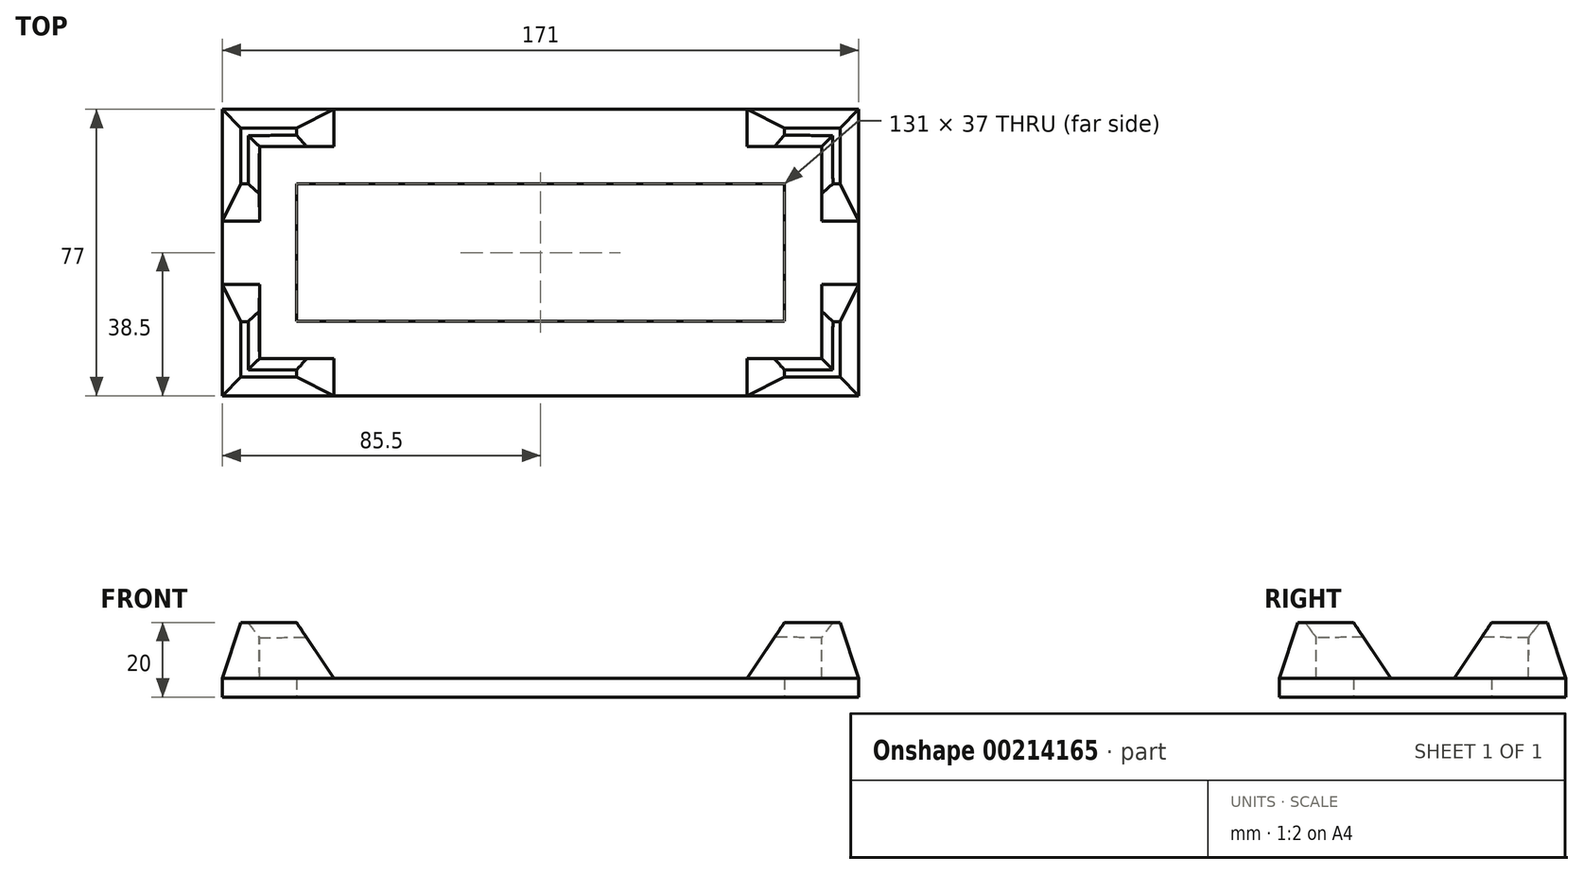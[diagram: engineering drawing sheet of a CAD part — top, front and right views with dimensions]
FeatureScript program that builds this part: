
annotation { "Feature Type Name" : "Feature", "Feature Type Description" : "" }
export const myFeature = defineFeature(function(context is Context, id is Id, definition is map)
    precondition{}
    {
        {
            var Q0;
            Q0=qCreatedBy(makeId("Top.planeOp"),FACE);
            var sketch = newSketch(context, id + "F0", { "sketchPlane" : qUnion([Q0])});
            skLineSegment(sketch, "E0.bottom", {"start": v(75.5, -28.5) * mm, "end": v(-75.5, -28.5) * mm, "construction": true});
            skLineSegment(sketch, "E0.top", {"start": v(75.5, 28.5) * mm, "end": v(-75.5, 28.5) * mm, "construction": true});
            skLineSegment(sketch, "E0.left", {"start": v(75.5, -28.5) * mm, "end": v(75.5, 28.5) * mm, "construction": true});
            skLineSegment(sketch, "E0.right", {"start": v(-75.5, -28.5) * mm, "end": v(-75.5, 28.5) * mm, "construction": true});
            skPoint(sketch, "E0.middle", {"position": v(0, 0) * mm});
            skLineSegment(sketch, "E1.bottom", {"start": v(85.5, -38.5) * mm, "end": v(-85.5, -38.5) * mm});
            skLineSegment(sketch, "E1.top", {"start": v(85.5, 38.5) * mm, "end": v(-85.5, 38.5) * mm});
            skLineSegment(sketch, "E1.left", {"start": v(85.5, -38.5) * mm, "end": v(85.5, 38.5) * mm});
            skLineSegment(sketch, "E1.right", {"start": v(-85.5, -38.5) * mm, "end": v(-85.5, 38.5) * mm});
            skSolve(sketch);
        }
        {
            var Q0;
            Q0=qCreatedBy(makeId("Top.planeOp"),FACE);
            cPlane(context, id + "F1", {"entities" : qUnion([Q0]), "cplaneType" : CPlaneType.OFFSET, "offset" : 15 * mm, "width" : 150 * mm, "height" : 150 * mm});
        }
        {
            var Q0;
            Q0=qCreatedBy(id+"F1.planeOp",FACE);
            var sketch = newSketch(context, id + "F2", { "sketchPlane" : qUnion([Q0])});
            skPoint(sketch, "E2.0", {"position": v(-85.5, -38.5) * mm});
            skPoint(sketch, "E3.0", {"position": v(-75.5, -28.5) * mm});
            skLineSegment(sketch, "E4", {"start": v(-75.58, -18.5) * mm, "end": v(-75.5, -28.5) * mm});
            skLineSegment(sketch, "E5", {"start": v(-75.5, -28.5) * mm, "end": v(-85.5, -38.5) * mm, "construction": true});
            skPoint(sketch, "E6", {"position": v(-80.5, -33.5) * mm});
            skLineSegment(sketch, "E7", {"start": v(-75.58, -18.5) * mm, "end": v(-80.5, -18.54) * mm});
            skLineSegment(sketch, "E8", {"start": v(-80.5, -18.54) * mm, "end": v(-80.5, -33.5) * mm});
            skLineSegment(sketch, "E9.MirrorCS", {"start": v(-65.54, -33.5) * mm, "end": v(-80.5, -33.5) * mm});
            skLineSegment(sketch, "E10.MirrorCS", {"start": v(-65.5, -28.58) * mm, "end": v(-65.54, -33.5) * mm});
            skLineSegment(sketch, "E11.MirrorCS", {"start": v(-65.5, -28.58) * mm, "end": v(-75.5, -28.5) * mm});
            skSolve(sketch);
        }
        {
            var Q0;
            Q0=qCreatedBy(makeId("Top.planeOp"),FACE);
            var sketch = newSketch(context, id + "F3", { "sketchPlane" : qUnion([Q0])});
            skPoint(sketch, "E12.0", {"position": v(-85.5, -38.5) * mm});
            skPoint(sketch, "E13.0", {"position": v(-75.5, -28.5) * mm});
            skLineSegment(sketch, "E14", {"start": v(-85.5, -38.5) * mm, "end": v(-85.5, -8.5) * mm});
            skLineSegment(sketch, "E15", {"start": v(-85.5, -8.5) * mm, "end": v(-75.5, -8.5) * mm});
            skLineSegment(sketch, "E16", {"start": v(-75.5, -8.5) * mm, "end": v(-75.5, -28.5) * mm});
            skLineSegment(sketch, "E17", {"start": v(-75.5, -28.5) * mm, "end": v(-85.5, -38.5) * mm, "construction": true});
            skLineSegment(sketch, "E18.MirrorCS", {"start": v(-55.5, -28.5) * mm, "end": v(-75.5, -28.5) * mm});
            skLineSegment(sketch, "E19.MirrorCS", {"start": v(-85.5, -38.5) * mm, "end": v(-55.5, -38.5) * mm});
            skLineSegment(sketch, "E20.MirrorCS", {"start": v(-55.5, -38.5) * mm, "end": v(-55.5, -28.5) * mm});
            skSolve(sketch);
        }
        {
            var Q0;
            Q0=makeQuery(id+"F0.imprint","IMPRINT",FACE,{"disambiguationData":[TD([[makeQuery(id+"F0.imprint","IMPRINT",EDGE,{"derivedFrom":sQuery(id+"F0.wireOp",EDGE,"E1.bottom")}),-1.0]])]});
            extrude(context, id + "F4", {"entities" : qUnion([Q0]), "oppositeDirection" : true, "depth" : 5 * mm});
        }
        {
            var Q1;
            Q1=makeQuery(id+"F3.imprint","IMPRINT",FACE,{"disambiguationData":[TD([[makeQuery(id+"F3.imprint","IMPRINT",EDGE,{"derivedFrom":sQuery(id+"F3.wireOp",EDGE,"E14")}),-1.0]])]});
            var Q2;
            Q2=makeQuery(id+"F2.imprint","IMPRINT",FACE,{"disambiguationData":[TD([[makeQuery(id+"F2.imprint","IMPRINT",EDGE,{"derivedFrom":sQuery(id+"F2.wireOp",EDGE,"E4")}),-1.0]])]});
            loft(context, id + "F5", {"operationType" : NewBodyOperationType.ADD, "sheetProfilesArray" : [{ "sheetProfileEntities" : qUnion([Q1]) }, { "sheetProfileEntities" : qUnion([Q2]) }]});
        }
        {
            var Q0;
            Q0=makeQuery(id+"F5.opLoft","MID_CAP_EDGE",EDGE,{"disambiguationData":[OSD([sQuery(id+"F2.wireOp",EDGE,"E4"),sQuery(id+"F2.wireOp",EDGE,"E7"),sQuery(id+"F2.wireOp",EDGE,"E11.MirrorCS")])],"capPos":1.0});
            var Q1;
            Q1=makeQuery(id+"F5.opLoft","MID_CAP_EDGE",EDGE,{"disambiguationData":[OSD([sQuery(id+"F2.wireOp",EDGE,"E4"),sQuery(id+"F2.wireOp",EDGE,"E10.MirrorCS"),sQuery(id+"F2.wireOp",EDGE,"E11.MirrorCS")])],"capPos":1.0});
            chamfer(context, id + "F6", {"entities" : qUnion([Q0, Q1]), "chamferType" : ChamferType.TWO_OFFSETS, "width1" : 3 * mm, "oppositeDirection" : false, "width2" : 4 * mm, "tangentPropagation" : true});
        }
        {
            var Q0;
            Q0=makeQuery(id+"F4.opExtrude","SWEPT_BODY",BODY,{"disambiguationData":[OSD([sQuery(id+"F0.wireOp",EDGE,"E1.bottom"),sQuery(id+"F0.wireOp",EDGE,"E1.top"),sQuery(id+"F0.wireOp",EDGE,"E1.left"),sQuery(id+"F0.wireOp",EDGE,"E1.right")])]});
            var Q1;
            Q1=qCreatedBy(makeId("Right.planeOp"),FACE);
            mirror(context, id + "F7", {"operationType" : NewBodyOperationType.ADD, "entities" : qUnion([Q0]), "mirrorPlane" : qUnion([Q1])});
        }
        {
            var Q0;
            Q0=makeQuery(id+"F4.opExtrude","SWEPT_BODY",BODY,{"disambiguationData":[OSD([sQuery(id+"F0.wireOp",EDGE,"E1.bottom"),sQuery(id+"F0.wireOp",EDGE,"E1.top"),sQuery(id+"F0.wireOp",EDGE,"E1.left"),sQuery(id+"F0.wireOp",EDGE,"E1.right")])]});
            var Q1;
            Q1=qCreatedBy(makeId("Front.planeOp"),FACE);
            mirror(context, id + "F8", {"operationType" : NewBodyOperationType.ADD, "entities" : qUnion([Q0]), "mirrorPlane" : qUnion([Q1])});
        }
        {
            var Q0;
            Q0=qCreatedBy(makeId("Top.planeOp"),FACE);
            var sketch = newSketch(context, id + "F9", { "sketchPlane" : qUnion([Q0])});
            skLineSegment(sketch, "E21.bottom", {"start": v(65.5, -18.5) * mm, "end": v(-65.5, -18.5) * mm});
            skLineSegment(sketch, "E21.top", {"start": v(65.5, 18.5) * mm, "end": v(-65.5, 18.5) * mm});
            skLineSegment(sketch, "E21.left", {"start": v(65.5, -18.5) * mm, "end": v(65.5, 18.5) * mm});
            skLineSegment(sketch, "E21.right", {"start": v(-65.5, -18.5) * mm, "end": v(-65.5, 18.5) * mm});
            skPoint(sketch, "E21.middle", {"position": v(0, 0) * mm});
            skLineSegment(sketch, "E22.0", {"start": v(-75.5, -28.5) * mm, "end": v(-75.5, 28.5) * mm, "construction": true});
            skLineSegment(sketch, "E23.0", {"start": v(75.5, 28.5) * mm, "end": v(-75.5, 28.5) * mm, "construction": true});
            skSolve(sketch);
        }
        {
            var Q0;
            Q0 = qSketchRegion(id + "F9", true);
            extrude(context, id + "F10", {"entities" : qUnion([Q0]), "operationType" : NewBodyOperationType.REMOVE, "depth" : 25 * mm, "symmetric" : true});
        }
    });
